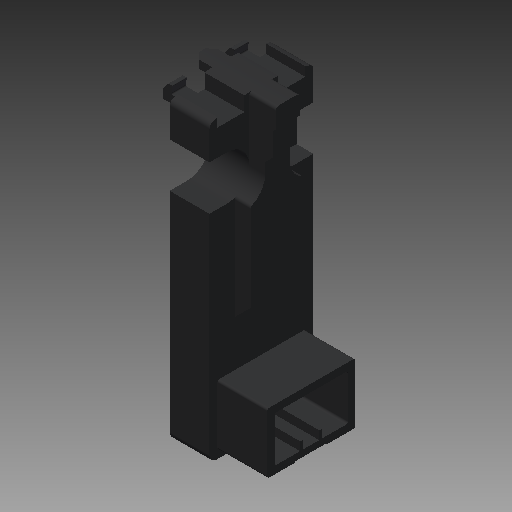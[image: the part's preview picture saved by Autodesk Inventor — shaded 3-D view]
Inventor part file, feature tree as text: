
AUTODESK INVENTOR PART (.ipt)
format: ipt  version: 2018 (Build 220112000, 112)  size: 274,944 bytes
history: native  units: mm
features: extrude x14, other x14, sketch x14
ambient origin geometry x8: Origin, YZ Plane, XZ Plane, XY Plane, X Axis, Y Axis, Z Axis, Center Point
bodies: Solid1 (feature_tree)
feature tree (42):
  extrude  "Extrusion1"  Depth=8.45mm TaperAngle=0.0deg
  extrude  "Extrusion2"  Depth=8.45mm TaperAngle=0.0deg
  extrude  "Extrusion3"  Depth=2.5mm TaperAngle=0.0deg
  extrude  "Extrusion4"  Depth=10.0mm TaperAngle=0.0deg
  extrude  "Extrusion5"  Depth=7.2mm TaperAngle=0.0deg
  extrude  "Extrusion6"  Depth=1.85mm TaperAngle=0.0deg
  extrude  "Extrusion7"  Depth=0.85mm TaperAngle=0.0deg
  extrude  "Extrusion8"  [1 undecoded]
  extrude  "Extrusion9"  [1 undecoded]
  extrude  "Extrusion10"  [1 undecoded]
  extrude  "Extrusion11"  [1 undecoded]
  extrude  "Extrusion12"  [1 undecoded]
  extrude  "Extrusion13"  [1 undecoded]
  extrude  "Extrusion14"  [1 undecoded]
  other  "NEBV_XY"
  other  "NEBV_YZ"
  other  "NEBV_ZX"
  other  "NEBV_X"
  other  "NEBV_Y"
  other  "NEBV_Z"
  other  "NEBV_Center"
  other  "VAVE_XY"
  other  "VAVE_YZ"
  other  "VAVE_ZX"
  other  "VAVE_X"
  other  "VAVE_Y"
  other  "VAVE_Z"
  other  "VAVE_Center"
  sketch  "Sketch_1"  dims[d0=8.45mm d1=0.0mm d2=8.45mm d3=0.0mm]
  sketch  "Sketch_2"  dims[d4=8.45mm d5=0.0mm d6=8.45mm d7=0.0mm]
  sketch  "Sketch_3"  dims[d8=8.45mm d9=0.0mm d10=2.5mm d11=0.0mm]
  sketch  "Sketch_4"  dims[d12=6.0mm d13=0.0mm d14=10.0mm d15=0.0mm]
  sketch  "Sketch_5"  dims[d16=3.0mm d17=0.0mm d18=7.2mm d19=0.0mm]
  sketch  "Sketch_7"  dims[d24=30.0mm d25=0.0mm d26=0.85mm d27=0.0mm]
  sketch  "Sketch_8"
  sketch  "Sketch_6"  dims[d20=30.0mm d21=0.0mm d22=1.85mm d23=0.0mm]
  sketch  "Sketch_9"
  sketch  "Sketch_13"
  sketch  "Sketch_14"
  sketch  "Sketch_11"
  sketch  "Sketch_10"
  sketch  "Sketch_12"
note: 7 required parameter values undecoded (feature->parameter linkage not recoverable at this tier; creation-order binding heuristic only, values carry confidence <= 0.55)
